# Revit family: CEL-Surface
name_source: partatom
category: Lighting Fixtures
units: mm (PartAtom-declared; Revit-internal decimal feet)

## family parameters
Cut with Voids When Loaded = No
Host = Face
Light Source = No
OmniClass Number = 23.80.70.11.21
OmniClass Title = Emergency Lighting
Part Type = Normal
Room Calculation Point = No
Round Connector Dimension = Use Diameter
Shared = No

## types (4) — shared parameters
Apparent Load = 4 VA
Default Elevation = 48.000"
Finish = White
Holder Material = Steel
Lamp = LED Lamp
Load Classification = Lighting
Manufacturer = Compass Products
URL = https://www.currentlighting.com
Wall Plate Material = Black
Wattage Comments = 3.72 W
Watts = 4 W

## per-type parameters (varying)
| type | Description | Lens | Model |
| CELS1RNE | Surface Mount, Single Face, Red Letters, Brushed Aluminum with Battery | Red Glass | CELS1RNE |
| CELS1GNE | Surface Mount, Single Face, Green Letters, Brushed Aluminum with Battery | Green Glass | CELS1RNE |
| CELS2RNE | Surface Mount, Double Face, Red Letters, Brushed Aluminum with Battery | Red Glass | CELS2RNE |
| CELS2GNE | Surface Mount, Double Face, Green Letters, Brushed Aluminum with Battery | Green Glass | CELS2GNE |

## geometry (parser evidence)
native form markers: Blend x8, Sweep x6
no freeform markers — native parametric forms only
